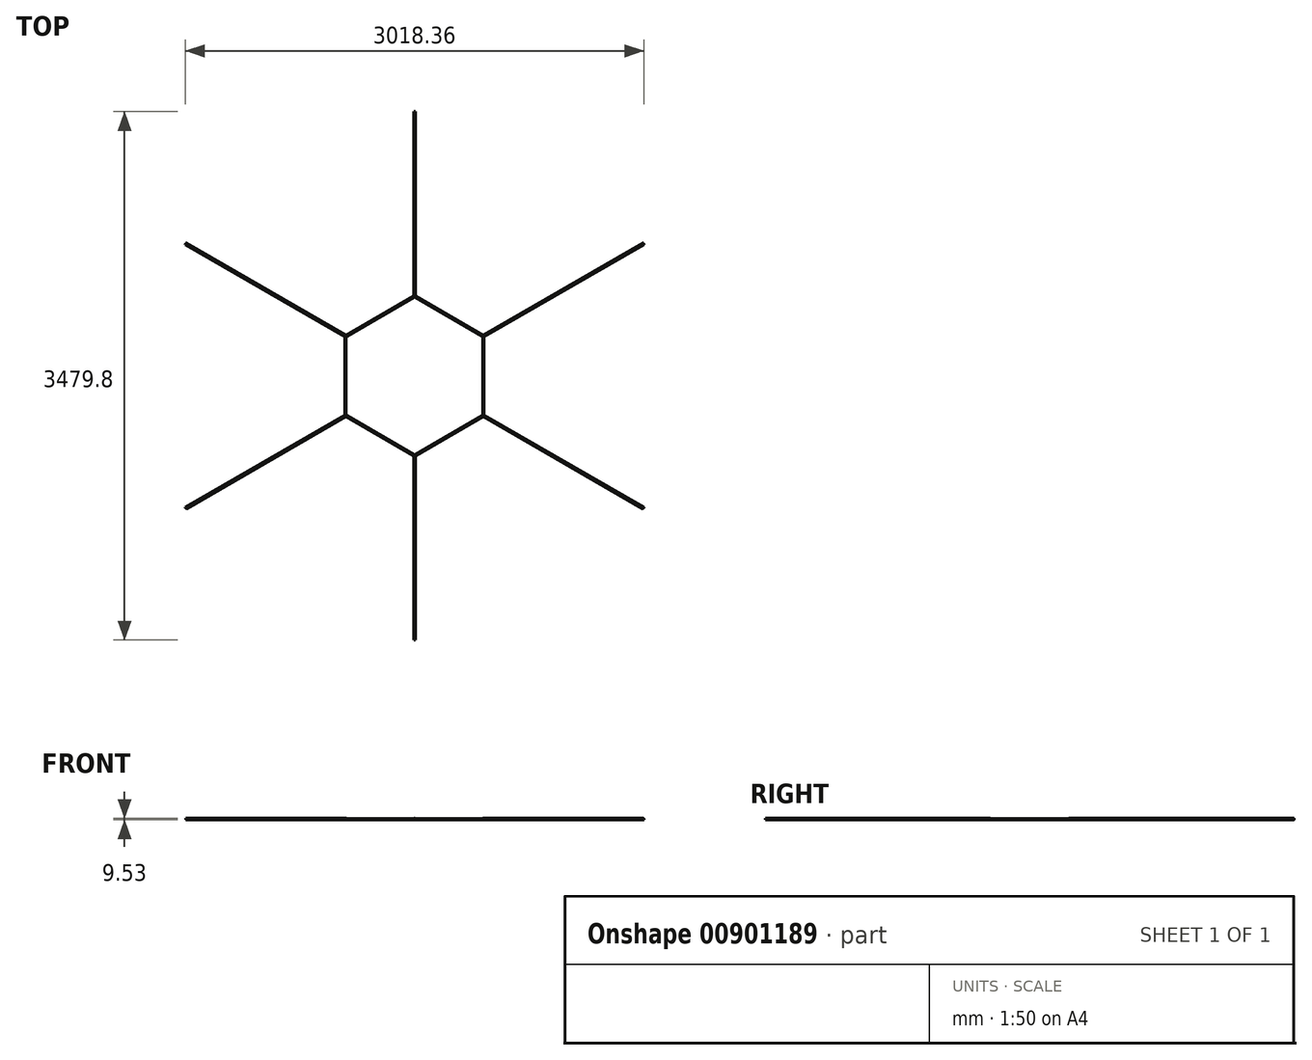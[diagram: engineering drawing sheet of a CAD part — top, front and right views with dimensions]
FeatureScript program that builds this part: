
annotation { "Feature Type Name" : "Feature", "Feature Type Description" : "" }
export const myFeature = defineFeature(function(context is Context, id is Id, definition is map)
    precondition{}
    {
        {
            var Q0;
            Q0=qCreatedBy(makeId("Top.planeOp"),FACE);
            var sketch = newSketch(context, id + "F0", { "sketchPlane" : qUnion([Q0])});
            skCircle(sketch, "E0.cCircle", {"center": v(0, 0) * mm, "radius": 457.2 * mm, "construction": true});
            skLineSegment(sketch, "E0.0", {"start": v(0, 527.93) * mm, "end": v(457.2, 263.96) * mm});
            skLineSegment(sketch, "E0.1", {"start": v(457.2, 263.96) * mm, "end": v(457.2, -263.96) * mm});
            skLineSegment(sketch, "E0.2", {"start": v(457.2, -263.96) * mm, "end": v(0, -527.93) * mm});
            skLineSegment(sketch, "E0.3", {"start": v(0, -527.93) * mm, "end": v(-457.2, -263.96) * mm});
            skLineSegment(sketch, "E0.4", {"start": v(-457.2, -263.96) * mm, "end": v(-457.2, 263.96) * mm});
            skLineSegment(sketch, "E0.5", {"start": v(-457.2, 263.96) * mm, "end": v(0, 527.93) * mm});
            skPoint(sketch, "E0.0.midPoint", {"position": v(228.6, 395.95) * mm});
            skCircle(sketch, "E1.cCircle", {"center": v(0, 0) * mm, "radius": 450.85 * mm, "construction": true});
            skLineSegment(sketch, "E1.0", {"start": v(0, 520.6) * mm, "end": v(450.85, 260.3) * mm});
            skLineSegment(sketch, "E1.1", {"start": v(450.85, 260.3) * mm, "end": v(450.85, -260.3) * mm});
            skLineSegment(sketch, "E1.2", {"start": v(450.85, -260.3) * mm, "end": v(0, -520.6) * mm});
            skLineSegment(sketch, "E1.3", {"start": v(0, -520.6) * mm, "end": v(-450.85, -260.3) * mm});
            skLineSegment(sketch, "E1.4", {"start": v(-450.85, -260.3) * mm, "end": v(-450.85, 260.3) * mm});
            skLineSegment(sketch, "E1.5", {"start": v(-450.85, 260.3) * mm, "end": v(0, 520.6) * mm});
            skPoint(sketch, "E1.0.midPoint", {"position": v(225.43, 390.45) * mm});
            skLineSegment(sketch, "E2", {"start": v(0, 0) * mm, "end": v(0, 624.87) * mm});
            skSolve(sketch);
        }
        {
            var Q0;
            Q0 = qSketchRegion(id + "F0", true);
            extrude(context, id + "F1", {"entities" : qUnion([Q0]), "depth" : 6.35 * mm, "offsetDistance" : 25.4 * mm});
        }
        {
            var Q0;
            Q0=qCreatedBy(makeId("Front.planeOp"),FACE);
            var sketch = newSketch(context, id + "F2", { "sketchPlane" : qUnion([Q0])});
            skCircle(sketch, "E3", {"center": v(0, 3.18) * mm, "radius": 4.76 * mm});
            skSolve(sketch);
        }
        {
            var Q0;
            Q0=makeQuery(id+"F2.imprint","IMPRINT",FACE,{"disambiguationData":[TD([[makeQuery(id+"F2.imprint","IMPRINT",EDGE,{"derivedFrom":sQuery(id+"F2.wireOp",EDGE,"E3")}),1.0]])]});
            extrude(context, id + "F3", {"entities" : qUnion([Q0]), "operationType" : NewBodyOperationType.ADD, "depth" : 1739.9 * mm, "offsetDistance" : 25.4 * mm});
        }
        {
            var Q0;
            Q0=qCreatedBy(makeId("Front.planeOp"),FACE);
            var sketch = newSketch(context, id + "F4", { "sketchPlane" : qUnion([Q0])});
            skLineSegment(sketch, "E4", {"start": v(0, 0) * mm, "end": v(0, 22.46) * mm});
            skSolve(sketch);
        }
        {
            var Q0;
            Q0=makeQuery(id+"F1.opExtrude","SWEPT_BODY",BODY,{"disambiguationData":[OSD([sQuery(id+"F0.wireOp",EDGE,"E0.0"),sQuery(id+"F0.wireOp",EDGE,"E0.1"),sQuery(id+"F0.wireOp",EDGE,"E0.2"),sQuery(id+"F0.wireOp",EDGE,"E0.3"),sQuery(id+"F0.wireOp",EDGE,"E0.4"),sQuery(id+"F0.wireOp",EDGE,"E0.5"),sQuery(id+"F0.wireOp",EDGE,"E1.0"),sQuery(id+"F0.wireOp",EDGE,"E1.1"),sQuery(id+"F0.wireOp",EDGE,"E1.2"),sQuery(id+"F0.wireOp",EDGE,"E1.3"),sQuery(id+"F0.wireOp",EDGE,"E1.4"),sQuery(id+"F0.wireOp",EDGE,"E1.5")])]});
            var Q1;
            Q1=sQuery(id+"F4.wireOp",EDGE,"E4");
            circularPattern(context, id + "F5", {"operationType" : NewBodyOperationType.ADD, "entities" : qUnion([Q0]), "axis" : qUnion([Q1]), "angle" : 360 * degree, "instanceCount" : 6, "equalSpace" : true});
        }
        {
            var Q0;
            Q0=qCreatedBy(makeId("Top.planeOp"),FACE);
            var sketch = newSketch(context, id + "F6", { "sketchPlane" : qUnion([Q0])});
            skCircle(sketch, "E5.cCircle", {"center": v(0, 0) * mm, "radius": 450.85 * mm, "construction": true});
            skLineSegment(sketch, "E5.0", {"start": v(450.85, 260.3) * mm, "end": v(450.85, -260.3) * mm});
            skLineSegment(sketch, "E5.1", {"start": v(450.85, -260.3) * mm, "end": v(0, -520.6) * mm});
            skLineSegment(sketch, "E5.2", {"start": v(0, -520.6) * mm, "end": v(-450.85, -260.3) * mm});
            skLineSegment(sketch, "E5.3", {"start": v(-450.85, -260.3) * mm, "end": v(-450.85, 260.3) * mm});
            skLineSegment(sketch, "E5.4", {"start": v(-450.85, 260.3) * mm, "end": v(0, 520.6) * mm});
            skLineSegment(sketch, "E5.5", {"start": v(0, 520.6) * mm, "end": v(450.85, 260.3) * mm});
            skPoint(sketch, "E5.0.midPoint", {"position": v(450.85, 0) * mm});
            skSolve(sketch);
        }
        {
            var Q0;
            Q0=makeQuery(id+"F6.imprint","IMPRINT",FACE,{"disambiguationData":[TD([[makeQuery(id+"F6.imprint","IMPRINT",EDGE,{"derivedFrom":sQuery(id+"F6.wireOp",EDGE,"E5.0")}),-1.0]])]});
            extrude(context, id + "F7", {"entities" : qUnion([Q0]), "operationType" : NewBodyOperationType.REMOVE, "oppositeDirection" : true, "depth" : 25.4 * mm, "offsetDistance" : 25.4 * mm, "hasSecondDirection" : true, "secondDirectionOppositeDirection" : false, "secondDirectionDepth" : 25.4 * mm});
        }
    });
